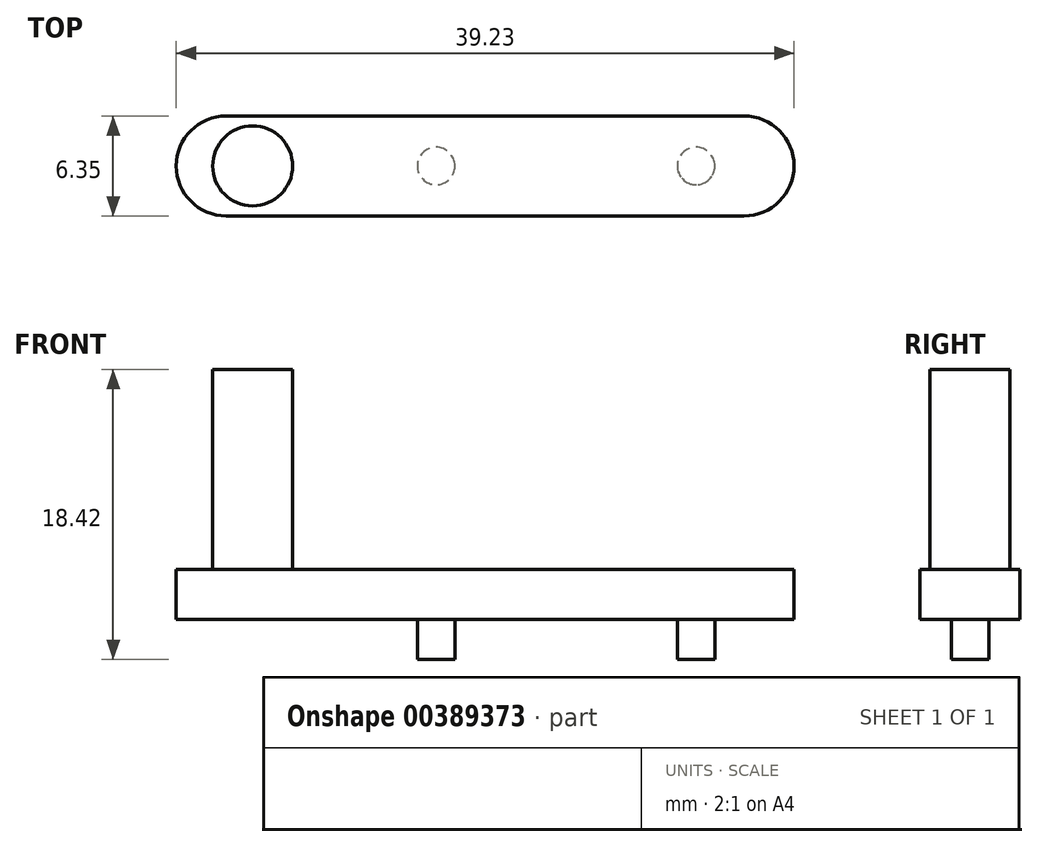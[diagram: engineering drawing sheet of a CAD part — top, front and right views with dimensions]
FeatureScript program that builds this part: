
annotation { "Feature Type Name" : "Feature", "Feature Type Description" : "" }
export const myFeature = defineFeature(function(context is Context, id is Id, definition is map)
    precondition{}
    {
        {
            var Q0;
            Q0=qCreatedBy(makeId("Top.planeOp"),FACE);
            var sketch = newSketch(context, id + "F0", { "sketchPlane" : qUnion([Q0])});
            skArc(sketch, "E0", {"start": v(0, 3.18) * mm, "mid": v(-3.18, 0) * mm, "end": v(0, -3.18) * mm});
            skArc(sketch, "E1", {"start": v(32.89, -3.18) * mm, "mid": v(36.06, 0) * mm, "end": v(32.89, 3.18) * mm});
            skLineSegment(sketch, "E2", {"start": v(0, 3.18) * mm, "end": v(32.89, 3.18) * mm});
            skLineSegment(sketch, "E3", {"start": v(0, -3.18) * mm, "end": v(32.89, -3.18) * mm});
            skSolve(sketch);
        }
        {
            var Q0;
            Q0 = qSketchRegion(id + "F0", true);
            extrude(context, id + "F1", {"entities" : qUnion([Q0]), "depth" : 3.17 * mm});
        }
        {
            var Q0;
            Q0=makeQuery(id+"F1.opExtrude","CAP_FACE",FACE,{"disambiguationData":[OSD([sQuery(id+"F0.wireOp",EDGE,"E0"),sQuery(id+"F0.wireOp",EDGE,"E1"),sQuery(id+"F0.wireOp",EDGE,"E2"),sQuery(id+"F0.wireOp",EDGE,"E3")])],"isStart":false});
            var sketch = newSketch(context, id + "F2", { "sketchPlane" : qUnion([Q0])});
            skCircle(sketch, "E4", {"center": v(1.68, 0) * mm, "radius": 2.54 * mm});
            skSolve(sketch);
        }
        {
            var Q0;
            Q0 = qSketchRegion(id + "F2", true);
            extrude(context, id + "F3", {"entities" : qUnion([Q0]), "operationType" : NewBodyOperationType.ADD, "depth" : 12.7 * mm});
        }
        {
            var Q0;
            Q0=makeQuery(id+"F1.opExtrude","CAP_FACE",FACE,{"disambiguationData":[OSD([sQuery(id+"F0.wireOp",EDGE,"E0"),sQuery(id+"F0.wireOp",EDGE,"E1"),sQuery(id+"F0.wireOp",EDGE,"E2"),sQuery(id+"F0.wireOp",EDGE,"E3")])],"isStart":true});
            var sketch = newSketch(context, id + "F4", { "sketchPlane" : qUnion([Q0])});
            skCircle(sketch, "E5", {"center": v(13.34, 0) * mm, "radius": 1.2 * mm});
            skCircle(sketch, "E6", {"center": v(29.85, 0) * mm, "radius": 1.2 * mm});
            skSolve(sketch);
        }
        {
            var Q0;
            Q0 = qSketchRegion(id + "F4", true);
            extrude(context, id + "F5", {"entities" : qUnion([Q0]), "operationType" : NewBodyOperationType.ADD, "depth" : 2.54 * mm});
        }
    });
